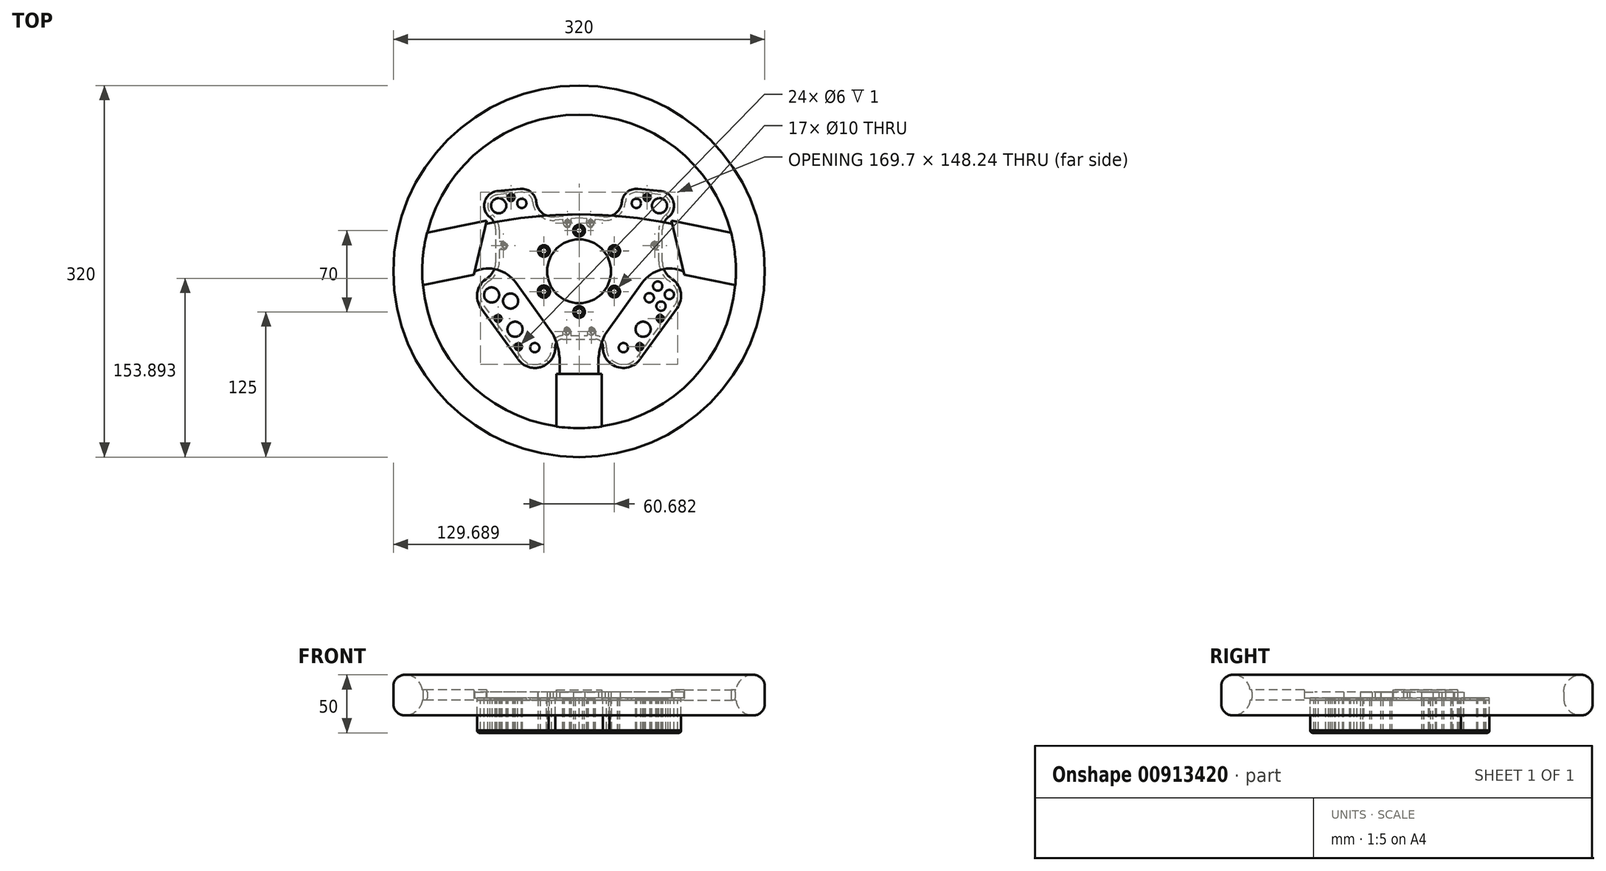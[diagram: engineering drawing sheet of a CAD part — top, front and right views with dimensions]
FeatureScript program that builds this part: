
annotation { "Feature Type Name" : "Feature", "Feature Type Description" : "" }
export const myFeature = defineFeature(function(context is Context, id is Id, definition is map)
    precondition{}
    {
        {
            var Q0;
            Q0=qCreatedBy(makeId("Top.planeOp"),FACE);
            cPlane(context, id + "F0", {"entities" : qUnion([Q0]), "cplaneType" : CPlaneType.OFFSET, "offset" : 0 * mm, "width" : 150 * mm, "height" : 150 * mm});
        }
        {
            var Q0;
            Q0=qCreatedBy(id+"F0.planeOp",FACE);
            var sketch = newSketch(context, id + "F1", { "sketchPlane" : qUnion([Q0])});
            skCircle(sketch, "E0", {"center": v(0, 0) * mm, "radius": 27.5 * mm});
            skCircle(sketch, "E1", {"center": v(0, 35) * mm, "radius": 5 * mm});
            skCircle(sketch, "E2", {"center": v(0, 35) * mm, "radius": 3 * mm});
            skCircle(sketch, "E3", {"center": v(30.31, 17.5) * mm, "radius": 5 * mm});
            skCircle(sketch, "E4", {"center": v(30.31, 17.5) * mm, "radius": 3 * mm});
            skCircle(sketch, "E5", {"center": v(-30.31, 17.5) * mm, "radius": 5 * mm});
            skCircle(sketch, "E6", {"center": v(-30.31, 17.5) * mm, "radius": 3 * mm});
            skCircle(sketch, "E7.MirrorC", {"center": v(-30.31, -17.5) * mm, "radius": 5.26 * mm});
            skCircle(sketch, "E8.MirrorC", {"center": v(-30.31, -17.5) * mm, "radius": 3 * mm});
            skCircle(sketch, "E9.MirrorC", {"center": v(0, -35) * mm, "radius": 5 * mm});
            skCircle(sketch, "E10.MirrorC", {"center": v(0, -35) * mm, "radius": 3 * mm});
            skCircle(sketch, "E11.MirrorC", {"center": v(30.31, -17.5) * mm, "radius": 5 * mm});
            skCircle(sketch, "E12.MirrorC", {"center": v(30.31, -17.5) * mm, "radius": 3 * mm});
            skLineSegment(sketch, "E13", {"start": v(90, 0) * mm, "end": v(80.2, 40.84) * mm});
            skPoint(sketch, "E14", {"position": v(0, -85.01) * mm});
            skPoint(sketch, "E15", {"position": v(38.44, -32.03) * mm});
            skLineSegment(sketch, "E16", {"start": v(38.44, -32.03) * mm, "end": v(54.55, -9.74) * mm});
            skLineSegment(sketch, "E17", {"start": v(38.44, -32.03) * mm, "end": v(22.33, -54.31) * mm});
            skArc(sketch, "E18", {"start": v(90, 0) * mm, "mid": v(70.56, 1.37) * mm, "end": v(54.55, -9.74) * mm});
            skLineSegment(sketch, "E19", {"start": v(16.6, -88.45) * mm, "end": v(16.6, -79.64) * mm});
            skArc(sketch, "E20", {"start": v(22.33, -54.31) * mm, "mid": v(18.06, -66.66) * mm, "end": v(16.6, -79.64) * mm});
            skLineSegment(sketch, "E21", {"start": v(0, 111.26) * mm, "end": v(0, -130.8) * mm});
            skLineSegment(sketch, "E22.MirrorCS", {"start": v(-90, 0) * mm, "end": v(-80.2, 40.84) * mm});
            skArc(sketch, "E23.MirrorCS", {"start": v(-90, 0) * mm, "mid": v(-70.56, 1.37) * mm, "end": v(-54.55, -9.74) * mm});
            skLineSegment(sketch, "E24.MirrorCS", {"start": v(-38.44, -32.03) * mm, "end": v(-54.55, -9.74) * mm});
            skLineSegment(sketch, "E25.MirrorCS", {"start": v(-38.44, -32.03) * mm, "end": v(-22.33, -54.31) * mm});
            skArc(sketch, "E26.MirrorCS", {"start": v(-22.33, -54.31) * mm, "mid": v(-18.06, -66.66) * mm, "end": v(-16.6, -79.64) * mm});
            skLineSegment(sketch, "E27", {"start": v(-16.6, -79.64) * mm, "end": v(-16.6, -88.45) * mm});
            skLineSegment(sketch, "E28", {"start": v(-16.6, -88.45) * mm, "end": v(16.6, -88.45) * mm});
            skPoint(sketch, "E29", {"position": v(0, 49) * mm});
            skArc(sketch, "E30", {"start": v(80.2, 40.84) * mm, "mid": v(0, 49) * mm, "end": v(-80.2, 40.84) * mm});
            skCircle(sketch, "E31", {"center": v(0, 0) * mm, "radius": 134.96 * mm});
            skCircle(sketch, "E32", {"center": v(0, 0) * mm, "radius": 160 * mm});
            skLineSegment(sketch, "E33", {"start": v(-80.2, 40.84) * mm, "end": v(-79.5, 43.76) * mm});
            skLineSegment(sketch, "E34", {"start": v(-79.5, 43.76) * mm, "end": v(-130.81, 33.2) * mm});
            skLineSegment(sketch, "E35", {"start": v(-90, 0) * mm, "end": v(-90.7, -2.92) * mm});
            skLineSegment(sketch, "E36", {"start": v(-90.7, -2.92) * mm, "end": v(-134.44, -11.9) * mm});
            skLineSegment(sketch, "E37.MirrorCS", {"start": v(79.5, 43.76) * mm, "end": v(130.81, 33.2) * mm});
            skLineSegment(sketch, "E38.MirrorCS", {"start": v(90.7, -2.92) * mm, "end": v(134.44, -11.9) * mm});
            skLineSegment(sketch, "E39.MirrorCS", {"start": v(90, 0) * mm, "end": v(90.7, -2.92) * mm});
            skLineSegment(sketch, "E40.MirrorCS", {"start": v(80.2, 40.84) * mm, "end": v(79.5, 43.76) * mm});
            skLineSegment(sketch, "E41", {"start": v(16.6, -88.45) * mm, "end": v(19.6, -88.45) * mm});
            skLineSegment(sketch, "E42", {"start": v(19.6, -88.45) * mm, "end": v(19.6, -133.53) * mm});
            skLineSegment(sketch, "E43", {"start": v(-16.6, -88.45) * mm, "end": v(-19.6, -88.45) * mm});
            skLineSegment(sketch, "E44", {"start": v(-19.6, -88.45) * mm, "end": v(-19.6, -133.53) * mm});
            skSolve(sketch);
        }
        {
            var Q0;
            Q0=makeQuery(id+"F1.imprint","IMPRINT",FACE,{"disambiguationData":[TD([[makeQuery(id+"F1.imprint","IMPRINT",EDGE,{"derivedFrom":sQuery(id+"F1.wireOp",EDGE,"E5")}),-1.0]])]});
            var Q1;
            Q1=makeQuery(id+"F1.imprint","IMPRINT",FACE,{"disambiguationData":[TD([[makeQuery(id+"F1.imprint","IMPRINT",EDGE,{"derivedFrom":sQuery(id+"F1.wireOp",EDGE,"E3")}),-1.0]])]});
            extrude(context, id + "F2", {"entities" : qUnion([Q0, Q1]), "endBound" : BoundingType.SYMMETRIC, "depth" : 5 * mm, "offsetDistance" : 25 * mm});
        }
        {
            var Q0;
            Q0=makeQuery(id+"F1.imprint","IMPRINT",FACE,{"disambiguationData":[TD([[makeQuery(id+"F1.imprint","IMPRINT",EDGE,{"derivedFrom":sQuery(id+"F1.wireOp",EDGE,"E22.MirrorCS")}),1.0]])]});
            var Q1;
            Q1=makeQuery(id+"F1.imprint","IMPRINT",FACE,{"disambiguationData":[TD([[makeQuery(id+"F1.imprint","IMPRINT",EDGE,{"derivedFrom":sQuery(id+"F1.wireOp",EDGE,"E13")}),-1.0]])]});
            var Q2;
            {var subQ0=sQuery(id+"F1.wireOp",EDGE,"biq8QzMH-OMzA-sGRV-lrNq-bHGwWP24Akrz");Q2=makeQuery(id+"F1.imprint","IMPRINT",FACE,{"disambiguationData":[TD([[makeQuery(id+"F1.imprint","IMPRINT",EDGE,{"derivedFrom":subQ0}),-1.0]])]});}
            var Q3;
            {var subQ0=sQuery(id+"F1.wireOp",EDGE,"E41");Q3=makeQuery(id+"F1.imprint","IMPRINT",FACE,{"disambiguationData":[TD([[makeQuery(id+"F1.imprint","IMPRINT",EDGE,{"derivedFrom":subQ0}),-1.0]])]});}
            extrude(context, id + "F3", {"entities" : qUnion([Q0, Q1, Q2, Q3]), "operationType" : NewBodyOperationType.ADD, "endBound" : BoundingType.SYMMETRIC, "depth" : 9 * mm, "offsetDistance" : 25 * mm});
        }
        {
            var Q0;
            Q0 = qSketchRegion(id + "F1", true);
            extrude(context, id + "F4", {"entities" : qUnion([Q0]), "operationType" : NewBodyOperationType.ADD, "endBound" : BoundingType.SYMMETRIC, "depth" : 35 * mm, "offsetDistance" : 25 * mm});
        }
        {
            var Q0;
            Q0=makeQuery(id+"F4.opExtrude","CAP_EDGE",EDGE,{"disambiguationData":[OSD([sQuery(id+"F1.wireOp",EDGE,"E32")])],"isStart":false});
            var Q1;
            Q1=makeQuery(id+"F4.opExtrude","CAP_EDGE",EDGE,{"disambiguationData":[OSD([sQuery(id+"F1.wireOp",EDGE,"E32")])],"isStart":true});
            fillet(context, id + "F5", {"entities" : qUnion([Q0, Q1]), "radius" : 10 * mm, "tangentPropagation" : true, "allowEdgeOverflow" : false});
        }
        {
            var Q0;
            Q0=makeQuery(id+"F4.opExtrude","CAP_EDGE",EDGE,{"disambiguationData":[OSD([sQuery(id+"F1.wireOp",EDGE,"E31")])],"isStart":false});
            var Q1;
            Q1=makeQuery(id+"F4.opExtrude","CAP_EDGE",EDGE,{"disambiguationData":[OSD([sQuery(id+"F1.wireOp",EDGE,"E31")])],"isStart":true});
            fillet(context, id + "F6", {"entities" : qUnion([Q0, Q1]), "radius" : 15 * mm, "tangentPropagation" : true, "allowEdgeOverflow" : false});
        }
        {
            var Q0;
            Q0=qCreatedBy(id+"F0.planeOp",FACE);
            cPlane(context, id + "F7", {"entities" : qUnion([Q0]), "cplaneType" : CPlaneType.OFFSET, "offset" : 2.5 * mm, "oppositeDirection" : true, "width" : 150 * mm, "height" : 150 * mm});
        }
        {
            var Q0;
            Q0=qCreatedBy(id+"F7.planeOp",FACE);
            var sketch = newSketch(context, id + "F8", { "sketchPlane" : qUnion([Q0])});
            skArc(sketch, "E45.0", {"start": v(36.9, 59.82) * mm, "mid": v(41.44, 68.24) * mm, "end": v(50.6, 71) * mm});
            skLineSegment(sketch, "E45.2", {"start": v(71.74, 35.7) * mm, "end": v(71.74, 8.37) * mm});
            skLineSegment(sketch, "E45.3", {"start": v(-14.23, -58.45) * mm, "end": v(0, -58.45) * mm});
            skLineSegment(sketch, "E45.5", {"start": v(-50.6, 71) * mm, "end": v(-70.5, 68.97) * mm});
            skArc(sketch, "E45.7", {"start": v(-36.9, 59.82) * mm, "mid": v(-41.44, 68.24) * mm, "end": v(-50.6, 71) * mm});
            skLineSegment(sketch, "E45.8", {"start": v(14.23, -58.45) * mm, "end": v(0, -58.45) * mm});
            skLineSegment(sketch, "E45.10", {"start": v(50.6, 71) * mm, "end": v(70.5, 68.97) * mm});
            skArc(sketch, "E45.11", {"start": v(-36.9, 59.82) * mm, "mid": v(-31.64, 50.05) * mm, "end": v(-21, 46.86) * mm});
            skArc(sketch, "E45.12", {"start": v(-80.6, -6.98) * mm, "mid": v(-87.64, -18.38) * mm, "end": v(-84.54, -31.42) * mm});
            skArc(sketch, "E45.13", {"start": v(-78.99, -5.8) * mm, "mid": v(-73.66, 0.4) * mm, "end": v(-71.74, 8.37) * mm});
            skArc(sketch, "E45.14", {"start": v(78.99, -5.8) * mm, "mid": v(73.66, 0.4) * mm, "end": v(71.74, 8.37) * mm});
            skLineSegment(sketch, "E45.15", {"start": v(-52.32, -75.99) * mm, "end": v(-84.54, -31.42) * mm});
            skLineSegment(sketch, "E45.16", {"start": v(-71.74, 35.7) * mm, "end": v(-71.74, 8.37) * mm});
            skArc(sketch, "E45.17", {"start": v(-70.5, 68.97) * mm, "mid": v(-78.92, 64.43) * mm, "end": v(-81.67, 55.27) * mm});
            skArc(sketch, "E45.18", {"start": v(36.9, 59.82) * mm, "mid": v(31.64, 50.05) * mm, "end": v(21, 46.86) * mm});
            skLineSegment(sketch, "E45.25", {"start": v(0, 40) * mm, "end": v(0, 49) * mm});
            skArc(sketch, "E45.26", {"start": v(70.5, 68.97) * mm, "mid": v(78.92, 64.43) * mm, "end": v(81.67, 55.27) * mm});
            skArc(sketch, "E45.27", {"start": v(52.32, -75.99) * mm, "mid": v(40.92, -83.01) * mm, "end": v(27.88, -79.92) * mm});
            skLineSegment(sketch, "E45.28", {"start": v(52.32, -75.99) * mm, "end": v(84.54, -31.42) * mm});
            skArc(sketch, "E45.33", {"start": v(-52.32, -75.99) * mm, "mid": v(-40.92, -83.01) * mm, "end": v(-27.88, -79.92) * mm});
            skArc(sketch, "E45.35", {"start": v(80.6, -6.98) * mm, "mid": v(87.64, -18.38) * mm, "end": v(84.54, -31.42) * mm});
            skLineSegment(sketch, "E46", {"start": v(-80.6, -6.98) * mm, "end": v(-78.99, -5.8) * mm});
            skLineSegment(sketch, "E47", {"start": v(78.99, -5.8) * mm, "end": v(80.6, -6.98) * mm});
            skLineSegment(sketch, "E48", {"start": v(-27.88, -79.92) * mm, "end": v(-26.19, -78.7) * mm});
            skLineSegment(sketch, "E49", {"start": v(26.19, -78.7) * mm, "end": v(27.88, -79.92) * mm});
            skPoint(sketch, "E50", {"position": v(-30.31, 17.5) * mm});
            skPoint(sketch, "E51", {"position": v(0, 35) * mm});
            skPoint(sketch, "E52", {"position": v(30.37, 17.62) * mm});
            skPoint(sketch, "E53", {"position": v(30.31, -17.5) * mm});
            skPoint(sketch, "E54", {"position": v(0, -35) * mm});
            skPoint(sketch, "E55", {"position": v(-30.31, -17.5) * mm});
            skCircle(sketch, "E56", {"center": v(-30.31, 17.5) * mm, "radius": 5 * mm});
            skCircle(sketch, "E57", {"center": v(0, 35) * mm, "radius": 5 * mm});
            skCircle(sketch, "E58", {"center": v(30.37, 17.62) * mm, "radius": 5 * mm});
            skCircle(sketch, "E59", {"center": v(30.31, -17.5) * mm, "radius": 5 * mm});
            skCircle(sketch, "E60", {"center": v(0, -35) * mm, "radius": 5 * mm});
            skCircle(sketch, "E61", {"center": v(-30.31, -17.5) * mm, "radius": 5 * mm});
            skLineSegment(sketch, "E62", {"start": v(-21, 46.86) * mm, "end": v(0, 49) * mm});
            skArc(sketch, "E63", {"start": v(-81.67, 55.27) * mm, "mid": v(-80.12, 50.39) * mm, "end": v(-76.74, 46.54) * mm});
            skArc(sketch, "E64", {"start": v(-71.74, 35.7) * mm, "mid": v(-73.05, 41.67) * mm, "end": v(-76.74, 46.54) * mm});
            skArc(sketch, "E65.MirrorCS", {"start": v(71.74, 35.7) * mm, "mid": v(73.05, 41.67) * mm, "end": v(76.74, 46.54) * mm});
            skArc(sketch, "E66.MirrorCS", {"start": v(81.67, 55.27) * mm, "mid": v(80.12, 50.39) * mm, "end": v(76.74, 46.54) * mm});
            skLineSegment(sketch, "E67.MirrorCS", {"start": v(21, 46.86) * mm, "end": v(0, 49) * mm});
            skArc(sketch, "E68", {"start": v(26.19, -78.7) * mm, "mid": v(22, -72.8) * mm, "end": v(20.51, -65.74) * mm});
            skArc(sketch, "E69", {"start": v(20.51, -65.74) * mm, "mid": v(19.04, -60.66) * mm, "end": v(14.23, -58.45) * mm});
            skArc(sketch, "E70.MirrorCS", {"start": v(-20.51, -65.74) * mm, "mid": v(-19.04, -60.66) * mm, "end": v(-14.23, -58.45) * mm});
            skArc(sketch, "E71.MirrorCS", {"start": v(-26.19, -78.7) * mm, "mid": v(-22, -72.8) * mm, "end": v(-20.51, -65.74) * mm});
            skSolve(sketch);
        }
        {
            var Q0;
            Q0=qCreatedBy(id+"F7.planeOp",FACE);
            var sketch = newSketch(context, id + "F9", { "sketchPlane" : qUnion([Q0])});
            skCircle(sketch, "E72.0", {"center": v(69.23, 56.53) * mm, "radius": 6.5 * mm});
            skCircle(sketch, "E73.0", {"center": v(49.33, 58.56) * mm, "radius": 4 * mm});
            skCircle(sketch, "E74.0", {"center": v(-49.33, 58.56) * mm, "radius": 4 * mm});
            skCircle(sketch, "E75.0", {"center": v(-69.23, 56.53) * mm, "radius": 6.5 * mm});
            skPoint(sketch, "E76", {"position": v(-38.14, -65.74) * mm});
            skPoint(sketch, "E77", {"position": v(38.14, -65.74) * mm});
            skCircle(sketch, "E78", {"center": v(-38.14, -65.74) * mm, "radius": 4 * mm});
            skCircle(sketch, "E79", {"center": v(38.14, -65.74) * mm, "radius": 4 * mm});
            skPoint(sketch, "E80", {"position": v(-27.88, -79.92) * mm});
            skPoint(sketch, "E81", {"position": v(-26.19, -78.7) * mm});
            skPoint(sketch, "E82", {"position": v(-78.99, -5.8) * mm});
            skPoint(sketch, "E83", {"position": v(-84.54, -31.42) * mm});
            skCircle(sketch, "E84", {"center": v(-75.3, -20.37) * mm, "radius": 6.5 * mm});
            skCircle(sketch, "E85", {"center": v(-58.99, -25.64) * mm, "radius": 6.5 * mm});
            skCircle(sketch, "E86", {"center": v(-55.18, -49.9) * mm, "radius": 6.5 * mm});
            skLineSegment(sketch, "E87", {"start": v(0, 72.77) * mm, "end": v(0, -121.4) * mm});
            skCircle(sketch, "E88.MirrorC", {"center": v(55.18, -49.9) * mm, "radius": 6.5 * mm});
            skPoint(sketch, "E89", {"position": v(27.88, -79.92) * mm});
            skPoint(sketch, "E90", {"position": v(80.6, -6.98) * mm});
            skPoint(sketch, "E91", {"position": v(84.54, -31.42) * mm});
            skArc(sketch, "E92", {"start": v(80.6, -6.98) * mm, "mid": v(87.64, -18.38) * mm, "end": v(84.54, -31.42) * mm});
            skLineSegment(sketch, "E93", {"start": v(87.64, -18.38) * mm, "end": v(81.71, -19.34) * mm});
            skLineSegment(sketch, "E94", {"start": v(81.71, -19.34) * mm, "end": v(73.81, -20.6) * mm});
            skCircle(sketch, "E95", {"center": v(77.76, -19.97) * mm, "radius": 4 * mm});
            skLineSegment(sketch, "E96", {"start": v(73.81, -20.6) * mm, "end": v(64.43, -22.12) * mm});
            skLineSegment(sketch, "E97", {"start": v(64.43, -22.12) * mm, "end": v(56.54, -23.39) * mm});
            skCircle(sketch, "E98", {"center": v(60.48, -22.75) * mm, "radius": 4 * mm});
            skLineSegment(sketch, "E99", {"start": v(69.12, -21.36) * mm, "end": v(68.37, -16.67) * mm});
            skLineSegment(sketch, "E100", {"start": v(68.37, -16.67) * mm, "end": v(67.1, -8.77) * mm});
            skLineSegment(sketch, "E101", {"start": v(69.12, -21.36) * mm, "end": v(69.88, -26.05) * mm});
            skLineSegment(sketch, "E102", {"start": v(69.88, -26.05) * mm, "end": v(71.15, -33.95) * mm});
            skCircle(sketch, "E103", {"center": v(67.73, -12.72) * mm, "radius": 4 * mm});
            skCircle(sketch, "E104", {"center": v(70.51, -30) * mm, "radius": 4 * mm});
            skSolve(sketch);
        }
        {
            var Q0;
            Q0=qCreatedBy(id+"F7.planeOp",FACE);
            var sketch = newSketch(context, id + "F10", { "sketchPlane" : qUnion([Q0])});
            skPoint(sketch, "E105", {"position": v(-65.2, 22.13) * mm});
            skPoint(sketch, "E106", {"position": v(-10, 41.4) * mm});
            skPoint(sketch, "E107", {"position": v(10, 41.4) * mm});
            skPoint(sketch, "E108", {"position": v(58.63, 63.6) * mm});
            skPoint(sketch, "E109", {"position": v(65.2, 22.13) * mm});
            skPoint(sketch, "E110", {"position": v(52.22, -64.97) * mm});
            skPoint(sketch, "E111", {"position": v(10.69, -51.91) * mm});
            skPoint(sketch, "E112", {"position": v(-10.69, -51.91) * mm});
            skPoint(sketch, "E113", {"position": v(-69.81, -40.63) * mm});
            skPoint(sketch, "E114", {"position": v(-58.63, 63.6) * mm});
            skPoint(sketch, "E115", {"position": v(-52.22, -64.97) * mm});
            skPoint(sketch, "E116", {"position": v(69.81, -40.63) * mm});
            skSolve(sketch);
        }
        {
            var Q0;
            Q0=qCreatedBy(id+"F7.planeOp",FACE);
            var sketch = newSketch(context, id + "F11", { "sketchPlane" : qUnion([Q0])});
            skPoint(sketch, "E117.0", {"position": v(-30.31, 17.5) * mm});
            skPoint(sketch, "E118.0", {"position": v(0, 35) * mm});
            skPoint(sketch, "E119.0", {"position": v(30.37, 17.62) * mm});
            skPoint(sketch, "E120.0", {"position": v(30.31, -17.5) * mm});
            skPoint(sketch, "E121.0", {"position": v(0, -35) * mm});
            skPoint(sketch, "E122.0", {"position": v(-30.31, -17.5) * mm});
            skCircle(sketch, "E123", {"center": v(-30.31, 17.5) * mm, "radius": 4.75 * mm});
            skCircle(sketch, "E124", {"center": v(0, 35) * mm, "radius": 4.75 * mm});
            skCircle(sketch, "E125", {"center": v(30.37, 17.62) * mm, "radius": 4.75 * mm});
            skCircle(sketch, "E126", {"center": v(30.31, -17.5) * mm, "radius": 4.75 * mm});
            skCircle(sketch, "E127", {"center": v(0, -35) * mm, "radius": 4.75 * mm});
            skCircle(sketch, "E128", {"center": v(-30.31, -17.5) * mm, "radius": 4.75 * mm});
            skCircle(sketch, "E129", {"center": v(-30.31, 17.5) * mm, "radius": 3 * mm});
            skCircle(sketch, "E130", {"center": v(0, 35) * mm, "radius": 3 * mm});
            skCircle(sketch, "E131", {"center": v(30.37, 17.62) * mm, "radius": 3 * mm});
            skCircle(sketch, "E132", {"center": v(30.31, -17.5) * mm, "radius": 3 * mm});
            skCircle(sketch, "E133", {"center": v(0, -35) * mm, "radius": 3 * mm});
            skCircle(sketch, "E134", {"center": v(-30.31, -17.5) * mm, "radius": 3 * mm});
            skSolve(sketch);
        }
        {
            var Q0;
            Q0 = qSketchRegion(id + "F8", true);
            extrude(context, id + "F12", {"entities" : qUnion([Q0]), "oppositeDirection" : true, "depth" : 2 * mm, "offsetDistance" : 25 * mm});
        }
        {
            var Q0;
            Q0=sQuery(id+"F8.wireOp",VERTEX,"E45.7.center");
            var Q1;
            Q1=sQuery(id+"F8.wireOp",VERTEX,"E45.0.center");
            var Q2;
            Q2=sQuery(id+"F9.wireOp",VERTEX,"036e1610-3aea-44eb-b534-3db68c6d7ca9.0.center");
            var Q3;
            Q3=sQuery(id+"F9.wireOp",VERTEX,"162f20b2-39f2-478e-86de-ea5148e8c145.0.center");
            var Q4;
            Q4=sQuery(id+"F9.wireOp",VERTEX,"decbba54-3b19-417b-ac4a-26fb6a5f3994.0.center");
            var Q5;
            Q5=sQuery(id+"F9.wireOp",VERTEX,"337ab1a7-4969-47b0-886a-c94dae99d71e.0.center");
            var Q6;
            Q6=sQuery(id+"F9.wireOp",VERTEX,"E77");
            var Q7;
            Q7=sQuery(id+"F9.wireOp",VERTEX,"E76");
            var Q8;
            Q8=sQuery(id+"F9.wireOp",VERTEX,"E95.center");
            var Q9;
            Q9=sQuery(id+"F9.wireOp",VERTEX,"E104.center");
            var Q10;
            Q10=sQuery(id+"F9.wireOp",VERTEX,"E98.center");
            var Q11;
            Q11=sQuery(id+"F9.wireOp",VERTEX,"E103.center");
            var Q12;
            Q12=makeQuery(id+"F12.opExtrude","SWEPT_BODY",BODY,{"disambiguationData":[OSD([sQuery(id+"F8.wireOp",EDGE,"E45.0"),sQuery(id+"F8.wireOp",EDGE,"E45.1"),sQuery(id+"F8.wireOp",EDGE,"E45.2"),sQuery(id+"F8.wireOp",EDGE,"E45.3"),sQuery(id+"F8.wireOp",EDGE,"E45.4"),sQuery(id+"F8.wireOp",EDGE,"E45.5"),sQuery(id+"F8.wireOp",EDGE,"E45.6"),sQuery(id+"F8.wireOp",EDGE,"E45.7"),sQuery(id+"F8.wireOp",EDGE,"E45.8"),sQuery(id+"F8.wireOp",EDGE,"E45.9"),sQuery(id+"F8.wireOp",EDGE,"E45.10"),sQuery(id+"F8.wireOp",EDGE,"E45.11"),sQuery(id+"F8.wireOp",EDGE,"E45.12"),sQuery(id+"F8.wireOp",EDGE,"E45.13"),sQuery(id+"F8.wireOp",EDGE,"E45.14"),sQuery(id+"F8.wireOp",EDGE,"E45.15"),sQuery(id+"F8.wireOp",EDGE,"E45.16"),sQuery(id+"F8.wireOp",EDGE,"E45.17"),sQuery(id+"F8.wireOp",EDGE,"E45.18"),sQuery(id+"F8.wireOp",EDGE,"E45.20"),sQuery(id+"F8.wireOp",EDGE,"E45.21"),sQuery(id+"F8.wireOp",EDGE,"E45.23"),sQuery(id+"F8.wireOp",EDGE,"E45.24"),sQuery(id+"F8.wireOp",EDGE,"E45.26"),sQuery(id+"F8.wireOp",EDGE,"E45.27"),sQuery(id+"F8.wireOp",EDGE,"E45.28"),sQuery(id+"F8.wireOp",EDGE,"E45.29"),sQuery(id+"F8.wireOp",EDGE,"E45.33"),sQuery(id+"F8.wireOp",EDGE,"E45.34"),sQuery(id+"F8.wireOp",EDGE,"E45.35"),sQuery(id+"F8.wireOp",EDGE,"E46"),sQuery(id+"F8.wireOp",EDGE,"E47"),sQuery(id+"F8.wireOp",EDGE,"E48"),sQuery(id+"F8.wireOp",EDGE,"E49"),sQuery(id+"F8.wireOp",EDGE,"E56"),sQuery(id+"F8.wireOp",EDGE,"E57"),sQuery(id+"F8.wireOp",EDGE,"E58"),sQuery(id+"F8.wireOp",EDGE,"E59"),sQuery(id+"F8.wireOp",EDGE,"E60"),sQuery(id+"F8.wireOp",EDGE,"E61")])]});
            hole(context, id + "F13", {"style" : HoleStyle.SIMPLE, "endStyle" : HoleEndStyle.BLIND, "holeDiameter" : 8 * mm, "majorDiameter" : 5 * mm, "holeDepth" : 4 * mm, "isTappedThrough" : true, "tappedDepth" : 12 * mm, "tapClearance" : 3, "locations" : qUnion([Q0, Q1, Q2, Q3, Q4, Q5, Q6, Q7, Q8, Q9, Q10, Q11]), "scope" : qUnion([Q12])});
        }
        {
            var Q0;
            Q0=sQuery(id+"F9.wireOp",VERTEX,"247b5355-b99b-4247-b5f6-1a5e020b961c.0.center");
            var Q1;
            Q1=sQuery(id+"F9.wireOp",VERTEX,"10302449-259c-4a36-9830-c1c0597fd3d2.0.center");
            var Q2;
            Q2=sQuery(id+"F9.wireOp",VERTEX,"78daf45b-b3f9-484f-a59a-663639ada313.0.center");
            var Q3;
            Q3=sQuery(id+"F9.wireOp",VERTEX,"7670e103-3e79-4102-925a-c4f0132792cc.0.center");
            var Q4;
            Q4=sQuery(id+"F8.wireOp",VERTEX,"E45.26.center");
            var Q5;
            Q5=sQuery(id+"F8.wireOp",VERTEX,"E45.17.center");
            var Q6;
            Q6=sQuery(id+"F9.wireOp",VERTEX,"E84.center");
            var Q7;
            Q7=sQuery(id+"F9.wireOp",VERTEX,"E85.center");
            var Q8;
            Q8=sQuery(id+"F9.wireOp",VERTEX,"E86.center");
            var Q9;
            Q9=sQuery(id+"F9.wireOp",VERTEX,"E88.MirrorC.center");
            var Q10;
            Q10=makeQuery(id+"F12.opExtrude","SWEPT_BODY",BODY,{"disambiguationData":[OSD([sQuery(id+"F8.wireOp",EDGE,"E45.0"),sQuery(id+"F8.wireOp",EDGE,"E45.1"),sQuery(id+"F8.wireOp",EDGE,"E45.2"),sQuery(id+"F8.wireOp",EDGE,"E45.3"),sQuery(id+"F8.wireOp",EDGE,"E45.4"),sQuery(id+"F8.wireOp",EDGE,"E45.5"),sQuery(id+"F8.wireOp",EDGE,"E45.6"),sQuery(id+"F8.wireOp",EDGE,"E45.7"),sQuery(id+"F8.wireOp",EDGE,"E45.8"),sQuery(id+"F8.wireOp",EDGE,"E45.9"),sQuery(id+"F8.wireOp",EDGE,"E45.10"),sQuery(id+"F8.wireOp",EDGE,"E45.11"),sQuery(id+"F8.wireOp",EDGE,"E45.12"),sQuery(id+"F8.wireOp",EDGE,"E45.13"),sQuery(id+"F8.wireOp",EDGE,"E45.14"),sQuery(id+"F8.wireOp",EDGE,"E45.15"),sQuery(id+"F8.wireOp",EDGE,"E45.16"),sQuery(id+"F8.wireOp",EDGE,"E45.17"),sQuery(id+"F8.wireOp",EDGE,"E45.18"),sQuery(id+"F8.wireOp",EDGE,"E45.20"),sQuery(id+"F8.wireOp",EDGE,"E45.21"),sQuery(id+"F8.wireOp",EDGE,"E45.23"),sQuery(id+"F8.wireOp",EDGE,"E45.24"),sQuery(id+"F8.wireOp",EDGE,"E45.26"),sQuery(id+"F8.wireOp",EDGE,"E45.27"),sQuery(id+"F8.wireOp",EDGE,"E45.28"),sQuery(id+"F8.wireOp",EDGE,"E45.29"),sQuery(id+"F8.wireOp",EDGE,"E45.33"),sQuery(id+"F8.wireOp",EDGE,"E45.34"),sQuery(id+"F8.wireOp",EDGE,"E45.35"),sQuery(id+"F8.wireOp",EDGE,"E46"),sQuery(id+"F8.wireOp",EDGE,"E47"),sQuery(id+"F8.wireOp",EDGE,"E48"),sQuery(id+"F8.wireOp",EDGE,"E49"),sQuery(id+"F8.wireOp",EDGE,"E56"),sQuery(id+"F8.wireOp",EDGE,"E57"),sQuery(id+"F8.wireOp",EDGE,"E58"),sQuery(id+"F8.wireOp",EDGE,"E59"),sQuery(id+"F8.wireOp",EDGE,"E60"),sQuery(id+"F8.wireOp",EDGE,"E61")])]});
            hole(context, id + "F14", {"style" : HoleStyle.SIMPLE, "endStyle" : HoleEndStyle.BLIND, "holeDiameter" : 13 * mm, "majorDiameter" : 5 * mm, "holeDepth" : 4 * mm, "isTappedThrough" : true, "tappedDepth" : 12 * mm, "tapClearance" : 3, "locations" : qUnion([Q0, Q1, Q2, Q3, Q4, Q5, Q6, Q7, Q8, Q9]), "scope" : qUnion([Q10])});
        }
        {
            var Q0;
            Q0=sQuery(id+"F18.wireOp",VERTEX,"E153.center");
            var Q1;
            Q1=sQuery(id+"F10.wireOp",VERTEX,"E105");
            var Q2;
            Q2=sQuery(id+"F10.wireOp",VERTEX,"E109");
            var Q3;
            Q3=sQuery(id+"F10.wireOp",VERTEX,"E108");
            var Q4;
            Q4=sQuery(id+"F10.wireOp",VERTEX,"E114");
            var Q5;
            Q5=sQuery(id+"F10.wireOp",VERTEX,"E110");
            var Q6;
            Q6=sQuery(id+"F10.wireOp",VERTEX,"E111");
            var Q7;
            Q7=sQuery(id+"F10.wireOp",VERTEX,"E112");
            var Q8;
            Q8=sQuery(id+"F10.wireOp",VERTEX,"E113");
            var Q9;
            Q9=sQuery(id+"F10.wireOp",VERTEX,"E106");
            var Q10;
            Q10=sQuery(id+"F10.wireOp",VERTEX,"E107");
            var Q11;
            Q11=sQuery(id+"F10.wireOp",VERTEX,"E115");
            var Q12;
            Q12=sQuery(id+"F10.wireOp",VERTEX,"E116");
            var Q13;
            Q13=makeQuery(id+"F12.opExtrude","SWEPT_BODY",BODY,{"disambiguationData":[OSD([sQuery(id+"F8.wireOp",EDGE,"E45.0"),sQuery(id+"F8.wireOp",EDGE,"E45.1"),sQuery(id+"F8.wireOp",EDGE,"E45.2"),sQuery(id+"F8.wireOp",EDGE,"E45.3"),sQuery(id+"F8.wireOp",EDGE,"E45.4"),sQuery(id+"F8.wireOp",EDGE,"E45.5"),sQuery(id+"F8.wireOp",EDGE,"E45.6"),sQuery(id+"F8.wireOp",EDGE,"E45.7"),sQuery(id+"F8.wireOp",EDGE,"E45.8"),sQuery(id+"F8.wireOp",EDGE,"E45.9"),sQuery(id+"F8.wireOp",EDGE,"E45.10"),sQuery(id+"F8.wireOp",EDGE,"E45.11"),sQuery(id+"F8.wireOp",EDGE,"E45.12"),sQuery(id+"F8.wireOp",EDGE,"E45.13"),sQuery(id+"F8.wireOp",EDGE,"E45.14"),sQuery(id+"F8.wireOp",EDGE,"E45.15"),sQuery(id+"F8.wireOp",EDGE,"E45.16"),sQuery(id+"F8.wireOp",EDGE,"E45.17"),sQuery(id+"F8.wireOp",EDGE,"E45.18"),sQuery(id+"F8.wireOp",EDGE,"E45.20"),sQuery(id+"F8.wireOp",EDGE,"E45.21"),sQuery(id+"F8.wireOp",EDGE,"E45.23"),sQuery(id+"F8.wireOp",EDGE,"E45.24"),sQuery(id+"F8.wireOp",EDGE,"E45.26"),sQuery(id+"F8.wireOp",EDGE,"E45.27"),sQuery(id+"F8.wireOp",EDGE,"E45.28"),sQuery(id+"F8.wireOp",EDGE,"E45.29"),sQuery(id+"F8.wireOp",EDGE,"E45.33"),sQuery(id+"F8.wireOp",EDGE,"E45.34"),sQuery(id+"F8.wireOp",EDGE,"E45.35"),sQuery(id+"F8.wireOp",EDGE,"E46"),sQuery(id+"F8.wireOp",EDGE,"E47"),sQuery(id+"F8.wireOp",EDGE,"E48"),sQuery(id+"F8.wireOp",EDGE,"E49"),sQuery(id+"F8.wireOp",EDGE,"E56"),sQuery(id+"F8.wireOp",EDGE,"E57"),sQuery(id+"F8.wireOp",EDGE,"E58"),sQuery(id+"F8.wireOp",EDGE,"E59"),sQuery(id+"F8.wireOp",EDGE,"E60"),sQuery(id+"F8.wireOp",EDGE,"E61")])]});
            hole(context, id + "F15", {"style" : HoleStyle.C_BORE, "endStyle" : HoleEndStyle.BLIND, "holeDiameter" : 3 * mm, "cBoreDiameter" : 6 * mm, "cBoreDepth" : 1 * mm, "majorDiameter" : 5 * mm, "holeDepth" : 2 * mm, "isTappedThrough" : true, "tappedDepth" : 12 * mm, "tapClearance" : 3, "locations" : qUnion([Q0, Q1, Q2, Q3, Q4, Q5, Q6, Q7, Q8, Q9, Q10, Q11, Q12]), "scope" : qUnion([Q13])});
        }
        {
            var Q0;
            Q0 = qSketchRegion(id + "F11", true);
            extrude(context, id + "F16", {"entities" : qUnion([Q0]), "oppositeDirection" : true, "depth" : 30 * mm, "offsetDistance" : 25 * mm});
        }
        {
            var Q0;
            Q0=qCreatedBy(id+"F7.planeOp",FACE);
            cPlane(context, id + "F17", {"entities" : qUnion([Q0]), "cplaneType" : CPlaneType.OFFSET, "offset" : 2 * mm, "oppositeDirection" : true, "width" : 150 * mm, "height" : 150 * mm});
        }
        {
            var Q0;
            Q0=qCreatedBy(id+"F17.planeOp",FACE);
            var sketch = newSketch(context, id + "F18", { "sketchPlane" : qUnion([Q0])});
            skLineSegment(sketch, "E135.0.19", {"start": v(0, -40) * mm, "end": v(0, -40) * mm});
            skLineSegment(sketch, "E135.0.21", {"start": v(0, -30) * mm, "end": v(0, -30) * mm});
            skArc(sketch, "E135.2.6", {"start": v(72.97, 1.92) * mm, "mid": v(72.05, 5.09) * mm, "end": v(71.74, 8.37) * mm});
            skLineSegment(sketch, "E135.2.7", {"start": v(71.74, 8.37) * mm, "end": v(71.74, 35.7) * mm});
            skLineSegment(sketch, "E135.2.11", {"start": v(21, 46.86) * mm, "end": v(0, 49) * mm});
            skLineSegment(sketch, "E135.2.19", {"start": v(0, -58.45) * mm, "end": v(14.23, -58.45) * mm});
            skArc(sketch, "E135.3.0", {"start": v(50.6, 71) * mm, "mid": v(41.44, 68.24) * mm, "end": v(36.9, 59.82) * mm});
            skArc(sketch, "E135.3.1", {"start": v(36.9, 59.82) * mm, "mid": v(34.18, 52.74) * mm, "end": v(28.27, 48) * mm});
            skArc(sketch, "E135.3.4", {"start": v(81.67, 55.27) * mm, "mid": v(78.92, 64.43) * mm, "end": v(70.5, 68.97) * mm});
            skLineSegment(sketch, "E135.3.5", {"start": v(70.5, 68.97) * mm, "end": v(50.6, 71) * mm});
            skArc(sketch, "E135.4.2", {"start": v(28.27, 48) * mm, "mid": v(24.7, 46.96) * mm, "end": v(21, 46.86) * mm});
            skLineSegment(sketch, "E135.5.1", {"start": v(26.19, -78.7) * mm, "end": v(27.88, -79.92) * mm});
            skArc(sketch, "E135.5.2", {"start": v(27.88, -79.92) * mm, "mid": v(40.92, -83.01) * mm, "end": v(52.32, -75.99) * mm});
            skLineSegment(sketch, "E135.5.3", {"start": v(52.32, -75.99) * mm, "end": v(84.54, -31.42) * mm});
            skArc(sketch, "E135.5.4", {"start": v(84.54, -31.42) * mm, "mid": v(87.64, -18.38) * mm, "end": v(80.6, -6.98) * mm});
            skLineSegment(sketch, "E135.5.5", {"start": v(80.6, -6.98) * mm, "end": v(79, -5.81) * mm});
            skArc(sketch, "E135.5.6", {"start": v(79, -5.81) * mm, "mid": v(75.43, -2.38) * mm, "end": v(72.97, 1.92) * mm});
            skLineSegment(sketch, "E136", {"start": v(0, 75.4) * mm, "end": v(0, -110.58) * mm});
            skArc(sketch, "E137.MirrorCS", {"start": v(-72.97, 1.92) * mm, "mid": v(-72.05, 5.09) * mm, "end": v(-71.74, 8.37) * mm});
            skArc(sketch, "E138.MirrorCS", {"start": v(-28.27, 48) * mm, "mid": v(-24.7, 46.96) * mm, "end": v(-21, 46.86) * mm});
            skLineSegment(sketch, "E139.MirrorCS", {"start": v(-80.6, -6.98) * mm, "end": v(-79, -5.81) * mm});
            skLineSegment(sketch, "E140.MirrorCS", {"start": v(-26.19, -78.7) * mm, "end": v(-27.88, -79.92) * mm});
            skArc(sketch, "E141.MirrorCS", {"start": v(-27.88, -79.92) * mm, "mid": v(-40.92, -83.01) * mm, "end": v(-52.32, -75.99) * mm});
            skArc(sketch, "E142.MirrorCS", {"start": v(-81.67, 55.27) * mm, "mid": v(-78.92, 64.43) * mm, "end": v(-70.5, 68.97) * mm});
            skArc(sketch, "E143.MirrorCS", {"start": v(-36.9, 59.82) * mm, "mid": v(-34.18, 52.74) * mm, "end": v(-28.27, 48) * mm});
            skLineSegment(sketch, "E144.MirrorCS", {"start": v(-52.32, -75.99) * mm, "end": v(-84.54, -31.42) * mm});
            skLineSegment(sketch, "E145.MirrorCS", {"start": v(-71.74, 8.37) * mm, "end": v(-71.74, 35.7) * mm});
            skLineSegment(sketch, "E146.MirrorCS", {"start": v(-70.5, 68.97) * mm, "end": v(-50.6, 71) * mm});
            skArc(sketch, "E147.MirrorCS", {"start": v(-84.54, -31.42) * mm, "mid": v(-87.64, -18.38) * mm, "end": v(-80.6, -6.98) * mm});
            skArc(sketch, "E148.MirrorCS", {"start": v(-50.6, 71) * mm, "mid": v(-41.44, 68.24) * mm, "end": v(-36.9, 59.82) * mm});
            skArc(sketch, "E149.MirrorCS", {"start": v(-79, -5.81) * mm, "mid": v(-75.43, -2.38) * mm, "end": v(-72.97, 1.92) * mm});
            skLineSegment(sketch, "E150.MirrorCS", {"start": v(-21, 46.86) * mm, "end": v(0, 49) * mm});
            skLineSegment(sketch, "E151.MirrorCS", {"start": v(0, -58.45) * mm, "end": v(-14.23, -58.45) * mm});
            skPoint(sketch, "E152", {"position": v(-68.74, 22.13) * mm});
            skCircle(sketch, "E153", {"center": v(-65.2, 22.13) * mm, "radius": 2.54 * mm});
            skArc(sketch, "E154", {"start": v(-65.2, 25.67) * mm, "mid": v(-61.66, 22.13) * mm, "end": v(-65.2, 18.59) * mm});
            skLineSegment(sketch, "E155", {"start": v(-65.2, 18.59) * mm, "end": v(-68.74, 18.59) * mm});
            skLineSegment(sketch, "E156", {"start": v(-65.2, 25.67) * mm, "end": v(-68.74, 25.67) * mm});
            skPoint(sketch, "E157", {"position": v(0, 45.98) * mm});
            skPoint(sketch, "E158", {"position": v(-10.35, 44.93) * mm});
            skPoint(sketch, "E159", {"position": v(10.35, 44.93) * mm});
            skLineSegment(sketch, "E160", {"start": v(-13.51, 41.05) * mm, "end": v(-13.87, 44.57) * mm});
            skLineSegment(sketch, "E161", {"start": v(-6.47, 41.77) * mm, "end": v(-6.83, 45.29) * mm});
            skCircle(sketch, "E162", {"center": v(-10, 41.4) * mm, "radius": 2.54 * mm});
            skArc(sketch, "E163", {"start": v(-13.51, 41.05) * mm, "mid": v(-9.63, 37.89) * mm, "end": v(-6.47, 41.77) * mm});
            skLineSegment(sketch, "E164", {"start": v(13.51, 41.05) * mm, "end": v(13.87, 44.57) * mm});
            skLineSegment(sketch, "E165", {"start": v(6.47, 41.77) * mm, "end": v(6.83, 45.29) * mm});
            skCircle(sketch, "E166", {"center": v(10, 41.4) * mm, "radius": 2.54 * mm});
            skArc(sketch, "E167", {"start": v(6.47, 41.77) * mm, "mid": v(9.63, 37.89) * mm, "end": v(13.51, 41.05) * mm});
            skLineSegment(sketch, "E168.MirrorCS", {"start": v(65.2, 25.67) * mm, "end": v(68.74, 25.67) * mm});
            skArc(sketch, "E169.MirrorCS", {"start": v(65.2, 25.67) * mm, "mid": v(61.66, 22.13) * mm, "end": v(65.2, 18.59) * mm});
            skCircle(sketch, "E170.MirrorC", {"center": v(65.2, 22.13) * mm, "radius": 2.54 * mm});
            skLineSegment(sketch, "E171.MirrorCS", {"start": v(65.2, 18.59) * mm, "end": v(68.74, 18.59) * mm});
            skPoint(sketch, "E172", {"position": v(-10.69, -55.45) * mm});
            skLineSegment(sketch, "E173", {"start": v(-14.23, -51.91) * mm, "end": v(-14.23, -55.45) * mm});
            skLineSegment(sketch, "E174", {"start": v(-7.15, -51.91) * mm, "end": v(-7.15, -55.45) * mm});
            skArc(sketch, "E175", {"start": v(-14.23, -51.91) * mm, "mid": v(-10.69, -48.37) * mm, "end": v(-7.15, -51.91) * mm});
            skCircle(sketch, "E176", {"center": v(-10.69, -51.91) * mm, "radius": 2.54 * mm});
            skArc(sketch, "E177.MirrorCS", {"start": v(14.23, -51.91) * mm, "mid": v(10.69, -48.37) * mm, "end": v(7.15, -51.91) * mm});
            skCircle(sketch, "E178.MirrorC", {"center": v(10.69, -51.91) * mm, "radius": 2.54 * mm});
            skLineSegment(sketch, "E179.MirrorCS", {"start": v(7.15, -51.91) * mm, "end": v(7.15, -55.45) * mm});
            skLineSegment(sketch, "E180.MirrorCS", {"start": v(14.23, -51.91) * mm, "end": v(14.23, -55.45) * mm});
            skPoint(sketch, "E181", {"position": v(-59, 67.12) * mm});
            skLineSegment(sketch, "E182", {"start": v(-55.11, 63.96) * mm, "end": v(-55.47, 67.48) * mm});
            skCircle(sketch, "E183", {"center": v(-58.63, 63.6) * mm, "radius": 2.54 * mm});
            skLineSegment(sketch, "E184", {"start": v(-62.16, 63.24) * mm, "end": v(-62.52, 66.76) * mm});
            skArc(sketch, "E185", {"start": v(-55.11, 63.96) * mm, "mid": v(-58.28, 60.08) * mm, "end": v(-62.16, 63.24) * mm});
            skLineSegment(sketch, "E186.MirrorCS", {"start": v(55.11, 63.96) * mm, "end": v(55.47, 67.48) * mm});
            skLineSegment(sketch, "E187.MirrorCS", {"start": v(62.16, 63.24) * mm, "end": v(62.52, 66.76) * mm});
            skCircle(sketch, "E188.MirrorC", {"center": v(58.63, 63.6) * mm, "radius": 2.54 * mm});
            skArc(sketch, "E189.MirrorCS", {"start": v(55.11, 63.96) * mm, "mid": v(58.28, 60.08) * mm, "end": v(62.16, 63.24) * mm});
            skPoint(sketch, "E190", {"position": v(57.17, -50.5) * mm});
            skCircle(sketch, "E191", {"center": v(52.22, -64.97) * mm, "radius": 2.54 * mm});
            skArc(sketch, "E192", {"start": v(54.3, -62.1) * mm, "mid": v(49.35, -62.9) * mm, "end": v(50.14, -67.84) * mm});
            skLineSegment(sketch, "E193", {"start": v(54.3, -62.1) * mm, "end": v(57.16, -64.17) * mm});
            skLineSegment(sketch, "E194", {"start": v(50.14, -67.84) * mm, "end": v(53.01, -69.91) * mm});
            skPoint(sketch, "E195", {"position": v(-55.18, -49.9) * mm});
            skPoint(sketch, "E196", {"position": v(-72.68, -42.7) * mm});
            skCircle(sketch, "E197", {"center": v(-69.81, -40.63) * mm, "radius": 2.54 * mm});
            skArc(sketch, "E198", {"start": v(-71.89, -37.76) * mm, "mid": v(-66.94, -38.55) * mm, "end": v(-67.74, -43.5) * mm});
            skLineSegment(sketch, "E199", {"start": v(-71.89, -37.76) * mm, "end": v(-74.76, -39.83) * mm});
            skLineSegment(sketch, "E200", {"start": v(-67.74, -43.5) * mm, "end": v(-70.6, -45.57) * mm});
            skArc(sketch, "E201.MirrorCS", {"start": v(71.89, -37.76) * mm, "mid": v(66.94, -38.55) * mm, "end": v(67.74, -43.5) * mm});
            skLineSegment(sketch, "E202.MirrorCS", {"start": v(71.89, -37.76) * mm, "end": v(74.76, -39.83) * mm});
            skLineSegment(sketch, "E203.MirrorCS", {"start": v(67.74, -43.5) * mm, "end": v(70.6, -45.57) * mm});
            skCircle(sketch, "E204.MirrorC", {"center": v(69.81, -40.63) * mm, "radius": 2.54 * mm});
            skLineSegment(sketch, "E205.MirrorCS", {"start": v(-50.14, -67.84) * mm, "end": v(-53.01, -69.91) * mm});
            skLineSegment(sketch, "E206.MirrorCS", {"start": v(-54.3, -62.1) * mm, "end": v(-57.16, -64.17) * mm});
            skArc(sketch, "E207.MirrorCS", {"start": v(-54.3, -62.1) * mm, "mid": v(-49.35, -62.9) * mm, "end": v(-50.14, -67.84) * mm});
            skCircle(sketch, "E208.MirrorC", {"center": v(-52.22, -64.97) * mm, "radius": 2.54 * mm});
            skPoint(sketch, "E209", {"position": v(-85.98, 35.7) * mm});
            skPoint(sketch, "E210", {"position": v(-76.74, 46.54) * mm});
            skPoint(sketch, "E211", {"position": v(-71.74, 35.7) * mm});
            skArc(sketch, "E212", {"start": v(-76.74, 46.54) * mm, "mid": v(-73.05, 41.67) * mm, "end": v(-71.74, 35.7) * mm});
            skArc(sketch, "E213", {"start": v(-81.67, 55.27) * mm, "mid": v(-80.12, 50.39) * mm, "end": v(-76.74, 46.54) * mm});
            skPoint(sketch, "E214", {"position": v(-14.23, -64.8) * mm});
            skPoint(sketch, "E215", {"position": v(-20.51, -65.74) * mm});
            skPoint(sketch, "E216", {"position": v(-14.23, -58.45) * mm});
            skArc(sketch, "E217", {"start": v(-14.23, -58.45) * mm, "mid": v(-19.04, -60.66) * mm, "end": v(-20.51, -65.74) * mm});
            skArc(sketch, "E218", {"start": v(-20.51, -65.74) * mm, "mid": v(-22, -72.8) * mm, "end": v(-26.19, -78.7) * mm});
            skLineSegment(sketch, "E219", {"start": v(-68.74, 25.67) * mm, "end": v(-68.74, 18.59) * mm});
            skLineSegment(sketch, "E220", {"start": v(-74.76, -39.83) * mm, "end": v(-70.6, -45.57) * mm});
            skLineSegment(sketch, "E221", {"start": v(-57.16, -64.17) * mm, "end": v(-53.01, -69.91) * mm});
            skLineSegment(sketch, "E222", {"start": v(-14.23, -55.45) * mm, "end": v(-7.15, -55.45) * mm});
            skLineSegment(sketch, "E223", {"start": v(7.15, -55.45) * mm, "end": v(14.23, -55.45) * mm});
            skLineSegment(sketch, "E224", {"start": v(53.01, -69.91) * mm, "end": v(57.16, -64.17) * mm});
            skLineSegment(sketch, "E225", {"start": v(70.6, -45.57) * mm, "end": v(74.76, -39.83) * mm});
            skLineSegment(sketch, "E226", {"start": v(68.74, 25.67) * mm, "end": v(68.74, 18.59) * mm});
            skLineSegment(sketch, "E227", {"start": v(62.52, 66.76) * mm, "end": v(55.47, 67.48) * mm});
            skLineSegment(sketch, "E228", {"start": v(13.87, 44.57) * mm, "end": v(6.83, 45.29) * mm});
            skLineSegment(sketch, "E229", {"start": v(-6.83, 45.29) * mm, "end": v(-13.87, 44.57) * mm});
            skLineSegment(sketch, "E230", {"start": v(-55.47, 67.48) * mm, "end": v(-62.52, 66.76) * mm});
            skArc(sketch, "E231.MirrorCS", {"start": v(14.23, -58.45) * mm, "mid": v(19.04, -60.66) * mm, "end": v(20.51, -65.74) * mm});
            skArc(sketch, "E232.MirrorCS", {"start": v(20.51, -65.74) * mm, "mid": v(22, -72.8) * mm, "end": v(26.19, -78.7) * mm});
            skArc(sketch, "E233.MirrorCS", {"start": v(76.74, 46.54) * mm, "mid": v(73.05, 41.67) * mm, "end": v(71.74, 35.7) * mm});
            skArc(sketch, "E234.MirrorCS", {"start": v(81.67, 55.27) * mm, "mid": v(80.12, 50.39) * mm, "end": v(76.74, 46.54) * mm});
            skArc(sketch, "E235.0", {"start": v(39.88, 59.52) * mm, "mid": v(33.53, 47.73) * mm, "end": v(20.7, 43.88) * mm});
            skArc(sketch, "E235.1", {"start": v(50.3, 68) * mm, "mid": v(43.33, 65.92) * mm, "end": v(39.88, 59.52) * mm});
            skLineSegment(sketch, "E235.2", {"start": v(70.2, 65.98) * mm, "end": v(50.3, 68) * mm});
            skArc(sketch, "E235.3", {"start": v(78.68, 55.57) * mm, "mid": v(76.6, 62.53) * mm, "end": v(70.2, 65.98) * mm});
            skArc(sketch, "E235.4", {"start": v(74.87, 48.89) * mm, "mid": v(77.48, 51.83) * mm, "end": v(78.68, 55.57) * mm});
            skArc(sketch, "E235.5", {"start": v(68.74, 35.7) * mm, "mid": v(70.35, 42.97) * mm, "end": v(74.87, 48.89) * mm});
            skLineSegment(sketch, "E235.6", {"start": v(68.74, 8.37) * mm, "end": v(68.74, 35.7) * mm});
            skArc(sketch, "E235.7", {"start": v(77.23, -8.24) * mm, "mid": v(70.99, -0.96) * mm, "end": v(68.74, 8.37) * mm});
            skLineSegment(sketch, "E235.8", {"start": v(78.85, -9.41) * mm, "end": v(77.23, -8.24) * mm});
            skArc(sketch, "E235.9", {"start": v(82.1, -29.66) * mm, "mid": v(84.67, -18.86) * mm, "end": v(78.85, -9.41) * mm});
            skLineSegment(sketch, "E235.10", {"start": v(49.89, -74.23) * mm, "end": v(82.1, -29.66) * mm});
            skLineSegment(sketch, "E235.11", {"start": v(-77.23, -8.24) * mm, "end": v(-78.85, -9.41) * mm});
            skArc(sketch, "E235.12", {"start": v(-68.74, 8.37) * mm, "mid": v(-70.99, -0.96) * mm, "end": v(-77.23, -8.24) * mm});
            skLineSegment(sketch, "E235.13", {"start": v(-68.74, 35.7) * mm, "end": v(-68.74, 8.37) * mm});
            skArc(sketch, "E235.14", {"start": v(-74.87, 48.89) * mm, "mid": v(-70.35, 42.97) * mm, "end": v(-68.74, 35.7) * mm});
            skArc(sketch, "E235.15", {"start": v(-78.68, 55.57) * mm, "mid": v(-77.48, 51.83) * mm, "end": v(-74.87, 48.89) * mm});
            skArc(sketch, "E235.16", {"start": v(-70.2, 65.98) * mm, "mid": v(-76.6, 62.53) * mm, "end": v(-78.68, 55.57) * mm});
            skLineSegment(sketch, "E235.17", {"start": v(0, 45.98) * mm, "end": v(-20.7, 43.88) * mm});
            skArc(sketch, "E235.18", {"start": v(-20.7, 43.88) * mm, "mid": v(-33.53, 47.73) * mm, "end": v(-39.88, 59.52) * mm});
            skArc(sketch, "E235.19", {"start": v(-39.88, 59.52) * mm, "mid": v(-43.33, 65.92) * mm, "end": v(-50.3, 68) * mm});
            skLineSegment(sketch, "E235.20", {"start": v(-50.3, 68) * mm, "end": v(-70.2, 65.98) * mm});
            skArc(sketch, "E235.21", {"start": v(-78.85, -9.41) * mm, "mid": v(-84.67, -18.86) * mm, "end": v(-82.1, -29.66) * mm});
            skLineSegment(sketch, "E235.22", {"start": v(-82.1, -29.66) * mm, "end": v(-49.89, -74.23) * mm});
            skArc(sketch, "E235.23", {"start": v(-49.89, -74.23) * mm, "mid": v(-40.44, -80.05) * mm, "end": v(-29.64, -77.49) * mm});
            skLineSegment(sketch, "E235.24", {"start": v(-29.64, -77.49) * mm, "end": v(-28.1, -76.37) * mm});
            skArc(sketch, "E235.25", {"start": v(-28.1, -76.37) * mm, "mid": v(-24.74, -71.61) * mm, "end": v(-23.51, -65.93) * mm});
            skArc(sketch, "E235.26", {"start": v(-23.51, -65.93) * mm, "mid": v(-21.23, -58.6) * mm, "end": v(-14.23, -55.45) * mm});
            skLineSegment(sketch, "E235.27", {"start": v(-14.23, -55.45) * mm, "end": v(0, -55.45) * mm});
            skLineSegment(sketch, "E235.28", {"start": v(0, -55.45) * mm, "end": v(14.23, -55.45) * mm});
            skArc(sketch, "E235.29", {"start": v(14.23, -55.45) * mm, "mid": v(21.23, -58.6) * mm, "end": v(23.51, -65.93) * mm});
            skArc(sketch, "E235.30", {"start": v(23.51, -65.93) * mm, "mid": v(24.74, -71.61) * mm, "end": v(28.1, -76.37) * mm});
            skLineSegment(sketch, "E235.31", {"start": v(28.1, -76.37) * mm, "end": v(29.64, -77.49) * mm});
            skLineSegment(sketch, "E235.32", {"start": v(20.7, 43.88) * mm, "end": v(0, 45.98) * mm});
            skArc(sketch, "E235.33", {"start": v(29.64, -77.49) * mm, "mid": v(40.44, -80.05) * mm, "end": v(49.89, -74.23) * mm});
            skSolve(sketch);
        }
        {
            var Q0;
            Q0 = qSketchRegion(id + "F18", true);
            var Q1;
            Q1=makeQuery(id+"F18.imprint","IMPRINT",FACE,{"disambiguationData":[TD([[makeQuery(id+"F18.imprint","IMPRINT",EDGE,{"derivedFrom":sQuery(id+"F18.wireOp",EDGE,"uIXX9VRL-GXcY-Oe1X-qzRk-8GKlFIXmTMJV")}),-1.0]])]});
            var Q2;
            Q2=makeQuery(id+"F18.imprint","IMPRINT",FACE,{"disambiguationData":[TD([[makeQuery(id+"F18.imprint","IMPRINT",EDGE,{"derivedFrom":sQuery(id+"F18.wireOp",EDGE,"E153")}),-1.0]])]});
            var Q3;
            {var subQ1=sQuery(id+"F18.wireOp",EDGE,"DaF0mra5-agkk-1JUC-BhPB-96Ip9KHHy1qw");Q3=makeQuery(id+"F18.imprint","IMPRINT",FACE,{"disambiguationData":[TD([[makeQuery(id+"F18.imprint","IMPRINT",EDGE,{"derivedFrom":subQ1}),-1.0]])]});}
            var Q4;
            Q4=makeQuery(id+"F18.imprint","IMPRINT",FACE,{"disambiguationData":[TD([[makeQuery(id+"F18.imprint","IMPRINT",EDGE,{"derivedFrom":sQuery(id+"F18.wireOp",EDGE,"HpCgtW3e-APvg-BcI5-VhwP-xPkz9Jsjn63X")}),-1.0]])]});
            var Q5;
            {var subQ1=sQuery(id+"F18.wireOp",EDGE,"E173");Q5=makeQuery(id+"F18.imprint","IMPRINT",FACE,{"disambiguationData":[TD([[makeQuery(id+"F18.imprint","IMPRINT",EDGE,{"derivedFrom":subQ1}),1.0]])]});}
            var Q6;
            Q6=makeQuery(id+"F18.imprint","IMPRINT",FACE,{"disambiguationData":[TD([[makeQuery(id+"F18.imprint","IMPRINT",EDGE,{"derivedFrom":sQuery(id+"F18.wireOp",EDGE,"E177.MirrorCS")}),1.0]])]});
            var Q7;
            {var subQ0=sQuery(id+"F18.wireOp",EDGE,"844f288c-ff90-4b92-a7f1-63b6584489fa0.MirrorCS");Q7=makeQuery(id+"F18.imprint","IMPRINT",FACE,{"disambiguationData":[TD([[makeQuery(id+"F18.imprint","IMPRINT",EDGE,{"derivedFrom":subQ0}),1.0]])]});}
            var Q8;
            {var subQ0=sQuery(id+"F18.wireOp",EDGE,"E168.MirrorCS");Q8=makeQuery(id+"F18.imprint","IMPRINT",FACE,{"disambiguationData":[TD([[makeQuery(id+"F18.imprint","IMPRINT",EDGE,{"derivedFrom":subQ0}),-1.0]])]});}
            var Q9;
            Q9=makeQuery(id+"F18.imprint","IMPRINT",FACE,{"disambiguationData":[TD([[makeQuery(id+"F18.imprint","IMPRINT",EDGE,{"derivedFrom":sQuery(id+"F18.wireOp",EDGE,"46ba9f76-3b62-4520-98e1-7f8efd3ca3140.MirrorCS")}),-1.0]])]});
            var Q10;
            {var subQ1=sQuery(id+"F18.wireOp",EDGE,"E164");Q10=makeQuery(id+"F18.imprint","IMPRINT",FACE,{"disambiguationData":[TD([[makeQuery(id+"F18.imprint","IMPRINT",EDGE,{"derivedFrom":subQ1}),1.0]])]});}
            var Q11;
            {var subQ1=sQuery(id+"F18.wireOp",EDGE,"E160");Q11=makeQuery(id+"F18.imprint","IMPRINT",FACE,{"disambiguationData":[TD([[makeQuery(id+"F18.imprint","IMPRINT",EDGE,{"derivedFrom":subQ1}),-1.0]])]});}
            var Q12;
            Q12=makeQuery(id+"F18.imprint","IMPRINT",FACE,{"disambiguationData":[TD([[makeQuery(id+"F18.imprint","IMPRINT",EDGE,{"derivedFrom":sQuery(id+"F18.wireOp",EDGE,"E191")}),-1.0]])]});
            var Q13;
            {var subQ0=sQuery(id+"F18.wireOp",EDGE,"E186.MirrorCS");Q13=makeQuery(id+"F18.imprint","IMPRINT",FACE,{"disambiguationData":[TD([[makeQuery(id+"F18.imprint","IMPRINT",EDGE,{"derivedFrom":subQ0}),-1.0]])]});}
            var Q14;
            {var subQ1=sQuery(id+"F18.wireOp",EDGE,"E182");Q14=makeQuery(id+"F18.imprint","IMPRINT",FACE,{"disambiguationData":[TD([[makeQuery(id+"F18.imprint","IMPRINT",EDGE,{"derivedFrom":subQ1}),1.0]])]});}
            var Q15;
            Q15=makeQuery(id+"F18.imprint","IMPRINT",FACE,{"disambiguationData":[TD([[makeQuery(id+"F18.imprint","IMPRINT",EDGE,{"derivedFrom":sQuery(id+"F18.wireOp",EDGE,"E197")}),-1.0]])]});
            var Q16;
            {var subQ1=sQuery(id+"F18.wireOp",EDGE,"E205.MirrorCS");Q16=makeQuery(id+"F18.imprint","IMPRINT",FACE,{"disambiguationData":[TD([[makeQuery(id+"F18.imprint","IMPRINT",EDGE,{"derivedFrom":subQ1}),-1.0]])]});}
            var Q17;
            Q17=makeQuery(id+"F18.imprint","IMPRINT",FACE,{"disambiguationData":[TD([[makeQuery(id+"F18.imprint","IMPRINT",EDGE,{"derivedFrom":sQuery(id+"F18.wireOp",EDGE,"E201.MirrorCS")}),1.0]])]});
            extrude(context, id + "F19", {"entities" : qUnion([Q0, Q1, Q2, Q3, Q4, Q5, Q6, Q7, Q8, Q9, Q10, Q11, Q12, Q13, Q14, Q15, Q16, Q17]), "oppositeDirection" : true, "depth" : (30 - 2 - 2) * mm, "offsetDistance" : 25 * mm});
        }
        {
            var Q0;
            Q0=qCreatedBy(id+"F17.planeOp",FACE);
            cPlane(context, id + "F20", {"entities" : qUnion([Q0]), "cplaneType" : CPlaneType.OFFSET, "offset" : 28 * mm, "oppositeDirection" : true, "width" : 150 * mm, "height" : 150 * mm});
        }
        {
            var Q0;
            Q0=qCreatedBy(id+"F20.planeOp",FACE);
            var sketch = newSketch(context, id + "F21", { "sketchPlane" : qUnion([Q0])});
            skArc(sketch, "E236.0", {"start": v(-70.5, 68.97) * mm, "mid": v(-78.92, 64.43) * mm, "end": v(-81.67, 55.27) * mm});
            skArc(sketch, "E236.1", {"start": v(80.6, -6.98) * mm, "mid": v(87.64, -18.38) * mm, "end": v(84.54, -31.42) * mm});
            skLineSegment(sketch, "E236.2", {"start": v(52.32, -75.99) * mm, "end": v(84.54, -31.42) * mm});
            skArc(sketch, "E236.4", {"start": v(-80.6, -6.98) * mm, "mid": v(-87.64, -18.38) * mm, "end": v(-84.54, -31.42) * mm});
            skLineSegment(sketch, "E236.7", {"start": v(50.6, 71) * mm, "end": v(70.5, 68.97) * mm});
            skArc(sketch, "E236.8", {"start": v(70.5, 68.97) * mm, "mid": v(78.92, 64.43) * mm, "end": v(81.67, 55.27) * mm});
            skLineSegment(sketch, "E236.10", {"start": v(-71.74, 35.7) * mm, "end": v(-71.74, 8.37) * mm});
            skArc(sketch, "E236.11", {"start": v(36.9, 59.82) * mm, "mid": v(41.44, 68.24) * mm, "end": v(50.6, 71) * mm});
            skArc(sketch, "E236.16", {"start": v(78.99, -5.8) * mm, "mid": v(73.66, 0.4) * mm, "end": v(71.74, 8.37) * mm});
            skLineSegment(sketch, "E236.21", {"start": v(-14.23, -58.45) * mm, "end": v(0, -58.45) * mm});
            skArc(sketch, "E236.23", {"start": v(-36.9, 59.82) * mm, "mid": v(-41.44, 68.24) * mm, "end": v(-50.6, 71) * mm});
            skLineSegment(sketch, "E236.24", {"start": v(71.74, 35.7) * mm, "end": v(71.74, 8.37) * mm});
            skArc(sketch, "E236.25", {"start": v(-36.9, 59.82) * mm, "mid": v(-31.64, 50.05) * mm, "end": v(-21, 46.86) * mm});
            skArc(sketch, "E236.26", {"start": v(36.9, 59.82) * mm, "mid": v(31.64, 50.05) * mm, "end": v(21, 46.86) * mm});
            skLineSegment(sketch, "E236.38", {"start": v(14.23, -58.45) * mm, "end": v(0, -58.45) * mm});
            skArc(sketch, "E236.40", {"start": v(52.32, -75.99) * mm, "mid": v(40.92, -83.01) * mm, "end": v(27.88, -79.92) * mm});
            skLineSegment(sketch, "E236.43", {"start": v(-52.32, -75.99) * mm, "end": v(-84.54, -31.42) * mm});
            skLineSegment(sketch, "E236.49", {"start": v(-50.6, 71) * mm, "end": v(-70.5, 68.97) * mm});
            skArc(sketch, "E236.51", {"start": v(-52.32, -75.99) * mm, "mid": v(-40.92, -83.01) * mm, "end": v(-27.88, -79.92) * mm});
            skArc(sketch, "E236.52", {"start": v(-78.99, -5.8) * mm, "mid": v(-73.66, 0.4) * mm, "end": v(-71.74, 8.37) * mm});
            skLineSegment(sketch, "E237", {"start": v(-80.6, -6.98) * mm, "end": v(-78.99, -5.8) * mm});
            skLineSegment(sketch, "E238", {"start": v(-27.88, -79.92) * mm, "end": v(-26.19, -78.7) * mm});
            skLineSegment(sketch, "E239", {"start": v(26.19, -78.7) * mm, "end": v(27.88, -79.92) * mm});
            skLineSegment(sketch, "E240", {"start": v(78.99, -5.8) * mm, "end": v(80.6, -6.98) * mm});
            skCircle(sketch, "E241", {"center": v(0, 35) * mm, "radius": 5 * mm});
            skCircle(sketch, "E242", {"center": v(30.31, 17.5) * mm, "radius": 5 * mm});
            skCircle(sketch, "E243", {"center": v(30.31, -17.5) * mm, "radius": 5 * mm});
            skCircle(sketch, "E244", {"center": v(0, -35) * mm, "radius": 5 * mm});
            skCircle(sketch, "E245", {"center": v(-30.31, -17.5) * mm, "radius": 5 * mm});
            skCircle(sketch, "E246", {"center": v(-30.31, 17.5) * mm, "radius": 5 * mm});
            skPoint(sketch, "E247", {"position": v(-85.98, 35.7) * mm});
            skPoint(sketch, "E248", {"position": v(-76.74, 46.54) * mm});
            skPoint(sketch, "E249", {"position": v(-14.23, -64.8) * mm});
            skPoint(sketch, "E250", {"position": v(-20.51, -65.74) * mm});
            skArc(sketch, "E251", {"start": v(-76.74, 46.54) * mm, "mid": v(-73.05, 41.67) * mm, "end": v(-71.74, 35.7) * mm});
            skArc(sketch, "E252", {"start": v(-76.74, 46.54) * mm, "mid": v(-80.12, 50.39) * mm, "end": v(-81.67, 55.27) * mm});
            skArc(sketch, "E253", {"start": v(-20.51, -65.74) * mm, "mid": v(-19.04, -60.66) * mm, "end": v(-14.23, -58.45) * mm});
            skArc(sketch, "E254", {"start": v(-20.51, -65.74) * mm, "mid": v(-22, -72.8) * mm, "end": v(-26.19, -78.7) * mm});
            skLineSegment(sketch, "E255", {"start": v(-21, 46.86) * mm, "end": v(0, 49) * mm});
            skLineSegment(sketch, "E256", {"start": v(0, 49) * mm, "end": v(21, 46.86) * mm});
            skArc(sketch, "E257.MirrorCS", {"start": v(76.74, 46.54) * mm, "mid": v(73.05, 41.67) * mm, "end": v(71.74, 35.7) * mm});
            skArc(sketch, "E258.MirrorCS", {"start": v(76.74, 46.54) * mm, "mid": v(80.12, 50.39) * mm, "end": v(81.67, 55.27) * mm});
            skArc(sketch, "E259.MirrorCS", {"start": v(20.51, -65.74) * mm, "mid": v(19.04, -60.66) * mm, "end": v(14.23, -58.45) * mm});
            skArc(sketch, "E260.MirrorCS", {"start": v(20.51, -65.74) * mm, "mid": v(22, -72.8) * mm, "end": v(26.19, -78.7) * mm});
            skSolve(sketch);
        }
        {
            var Q0;
            Q0 = qSketchRegion(id + "F21", true);
            extrude(context, id + "F22", {"entities" : qUnion([Q0]), "depth" : 2 * mm, "offsetDistance" : 25 * mm});
        }
        {
            var Q0;
            Q0=qCreatedBy(id+"F20.planeOp",FACE);
            var sketch = newSketch(context, id + "F23", { "sketchPlane" : qUnion([Q0])});
            skPoint(sketch, "E261", {"position": v(-69.81, -40.63) * mm});
            skPoint(sketch, "E262", {"position": v(-10.69, -51.91) * mm});
            skPoint(sketch, "E263", {"position": v(10.69, -51.91) * mm});
            skPoint(sketch, "E264", {"position": v(52.22, -64.97) * mm});
            skPoint(sketch, "E265", {"position": v(65.2, 22.13) * mm});
            skPoint(sketch, "E266", {"position": v(58.63, 63.6) * mm});
            skPoint(sketch, "E267", {"position": v(10, 41.4) * mm});
            skPoint(sketch, "E268", {"position": v(-10, 41.4) * mm});
            skPoint(sketch, "E269", {"position": v(-58.63, 63.6) * mm});
            skPoint(sketch, "E270", {"position": v(-65.2, 22.13) * mm});
            skPoint(sketch, "E271", {"position": v(-52.22, -64.97) * mm});
            skPoint(sketch, "E272", {"position": v(69.81, -40.63) * mm});
            skSolve(sketch);
        }
        {
            var Q0;
            Q0=sQuery(id+"F23.wireOp",VERTEX,"E262");
            var Q1;
            Q1=sQuery(id+"F23.wireOp",VERTEX,"E263");
            var Q2;
            Q2=sQuery(id+"F23.wireOp",VERTEX,"E267");
            var Q3;
            Q3=sQuery(id+"F23.wireOp",VERTEX,"E268");
            var Q4;
            Q4=sQuery(id+"F23.wireOp",VERTEX,"E266");
            var Q5;
            Q5=sQuery(id+"F23.wireOp",VERTEX,"E265");
            var Q6;
            Q6=sQuery(id+"F23.wireOp",VERTEX,"E264");
            var Q7;
            Q7=sQuery(id+"F23.wireOp",VERTEX,"E269");
            var Q8;
            Q8=sQuery(id+"F23.wireOp",VERTEX,"E270");
            var Q9;
            Q9=sQuery(id+"F23.wireOp",VERTEX,"E261");
            var Q10;
            Q10=sQuery(id+"F23.wireOp",VERTEX,"E271");
            var Q11;
            Q11=sQuery(id+"F23.wireOp",VERTEX,"E272");
            var Q12;
            Q12=makeQuery(id+"F22.opExtrude","SWEPT_BODY",BODY,{"disambiguationData":[OSD([sQuery(id+"F21.wireOp",EDGE,"E236.0"),sQuery(id+"F21.wireOp",EDGE,"E236.1"),sQuery(id+"F21.wireOp",EDGE,"E236.2"),sQuery(id+"F21.wireOp",EDGE,"E236.4"),sQuery(id+"F21.wireOp",EDGE,"E236.7"),sQuery(id+"F21.wireOp",EDGE,"E236.8"),sQuery(id+"F21.wireOp",EDGE,"E236.10"),sQuery(id+"F21.wireOp",EDGE,"E236.11"),sQuery(id+"F21.wireOp",EDGE,"E236.12"),sQuery(id+"F21.wireOp",EDGE,"E236.15"),sQuery(id+"F21.wireOp",EDGE,"E236.16"),sQuery(id+"F21.wireOp",EDGE,"E236.20"),sQuery(id+"F21.wireOp",EDGE,"E236.21"),sQuery(id+"F21.wireOp",EDGE,"E236.23"),sQuery(id+"F21.wireOp",EDGE,"E236.24"),sQuery(id+"F21.wireOp",EDGE,"E236.25"),sQuery(id+"F21.wireOp",EDGE,"E236.26"),sQuery(id+"F21.wireOp",EDGE,"E236.31"),sQuery(id+"F21.wireOp",EDGE,"E236.33"),sQuery(id+"F21.wireOp",EDGE,"E236.38"),sQuery(id+"F21.wireOp",EDGE,"E236.39"),sQuery(id+"F21.wireOp",EDGE,"E236.40"),sQuery(id+"F21.wireOp",EDGE,"E236.41"),sQuery(id+"F21.wireOp",EDGE,"E236.43"),sQuery(id+"F21.wireOp",EDGE,"E236.46"),sQuery(id+"F21.wireOp",EDGE,"E236.49"),sQuery(id+"F21.wireOp",EDGE,"E236.51"),sQuery(id+"F21.wireOp",EDGE,"E236.52"),sQuery(id+"F21.wireOp",EDGE,"oNHiE6x1-wNwA-23Tf-BYKf-yuz94zJXCFFU"),sQuery(id+"F21.wireOp",EDGE,"C15gbMUp-Su9s-5i6a-t6IC-VsMevMJijxky"),sQuery(id+"F21.wireOp",EDGE,"E237"),sQuery(id+"F21.wireOp",EDGE,"E238"),sQuery(id+"F21.wireOp",EDGE,"E239"),sQuery(id+"F21.wireOp",EDGE,"E240"),sQuery(id+"F21.wireOp",EDGE,"E241"),sQuery(id+"F21.wireOp",EDGE,"E242"),sQuery(id+"F21.wireOp",EDGE,"E243"),sQuery(id+"F21.wireOp",EDGE,"E244"),sQuery(id+"F21.wireOp",EDGE,"E245"),sQuery(id+"F21.wireOp",EDGE,"E246")])]});
            hole(context, id + "F24", {"style" : HoleStyle.C_BORE, "endStyle" : HoleEndStyle.BLIND, "oppositeDirection" : true, "holeDiameter" : 3 * mm, "cBoreDiameter" : 6 * mm, "cBoreDepth" : 1 * mm, "majorDiameter" : 5 * mm, "holeDepth" : 2 * mm, "isTappedThrough" : true, "tappedDepth" : 12 * mm, "tapClearance" : 3, "locations" : qUnion([Q0, Q1, Q2, Q3, Q4, Q5, Q6, Q7, Q8, Q9, Q10, Q11]), "scope" : qUnion([Q12])});
        }
        {
            var Q0;
            Q0=makeQuery(id+"F22.opExtrude","CAP_EDGE",EDGE,{"disambiguationData":[OSD([sQuery(id+"F21.wireOp",EDGE,"E236.43")])],"isStart":true});
            var Q1;
            Q1=makeQuery(id+"F22.opExtrude","CAP_EDGE",EDGE,{"disambiguationData":[OSD([sQuery(id+"F21.wireOp",EDGE,"E236.0"),sQuery(id+"F21.wireOp",EDGE,"E252")])],"isStart":true});
            var Q2;
            Q2=makeQuery(id+"F22.opExtrude","CAP_EDGE",EDGE,{"disambiguationData":[OSD([sQuery(id+"F21.wireOp",EDGE,"E236.2")])],"isStart":true});
            var Q3;
            Q3=makeQuery(id+"F22.opExtrude","CAP_EDGE",EDGE,{"disambiguationData":[OSD([sQuery(id+"F21.wireOp",EDGE,"E236.8"),sQuery(id+"F21.wireOp",EDGE,"E258.MirrorCS")])],"isStart":true});
            var Q4;
            Q4=makeQuery(id+"F22.opExtrude","CAP_EDGE",EDGE,{"disambiguationData":[OSD([sQuery(id+"F21.wireOp",EDGE,"E259.MirrorCS")])],"isStart":true});
            var Q5;
            Q5=makeQuery(id+"F22.opExtrude","CAP_EDGE",EDGE,{"disambiguationData":[OSD([sQuery(id+"F21.wireOp",EDGE,"E260.MirrorCS")])],"isStart":true});
            var Q6;
            Q6=makeQuery(id+"F22.opExtrude","CAP_EDGE",EDGE,{"disambiguationData":[OSD([sQuery(id+"F21.wireOp",EDGE,"E254")])],"isStart":true});
            fillet(context, id + "F25", {"entities" : qUnion([Q0, Q1, Q2, Q3, Q4, Q5, Q6]), "radius" : 2 * mm, "tangentPropagation" : true, "allowEdgeOverflow" : false});
        }
    });
